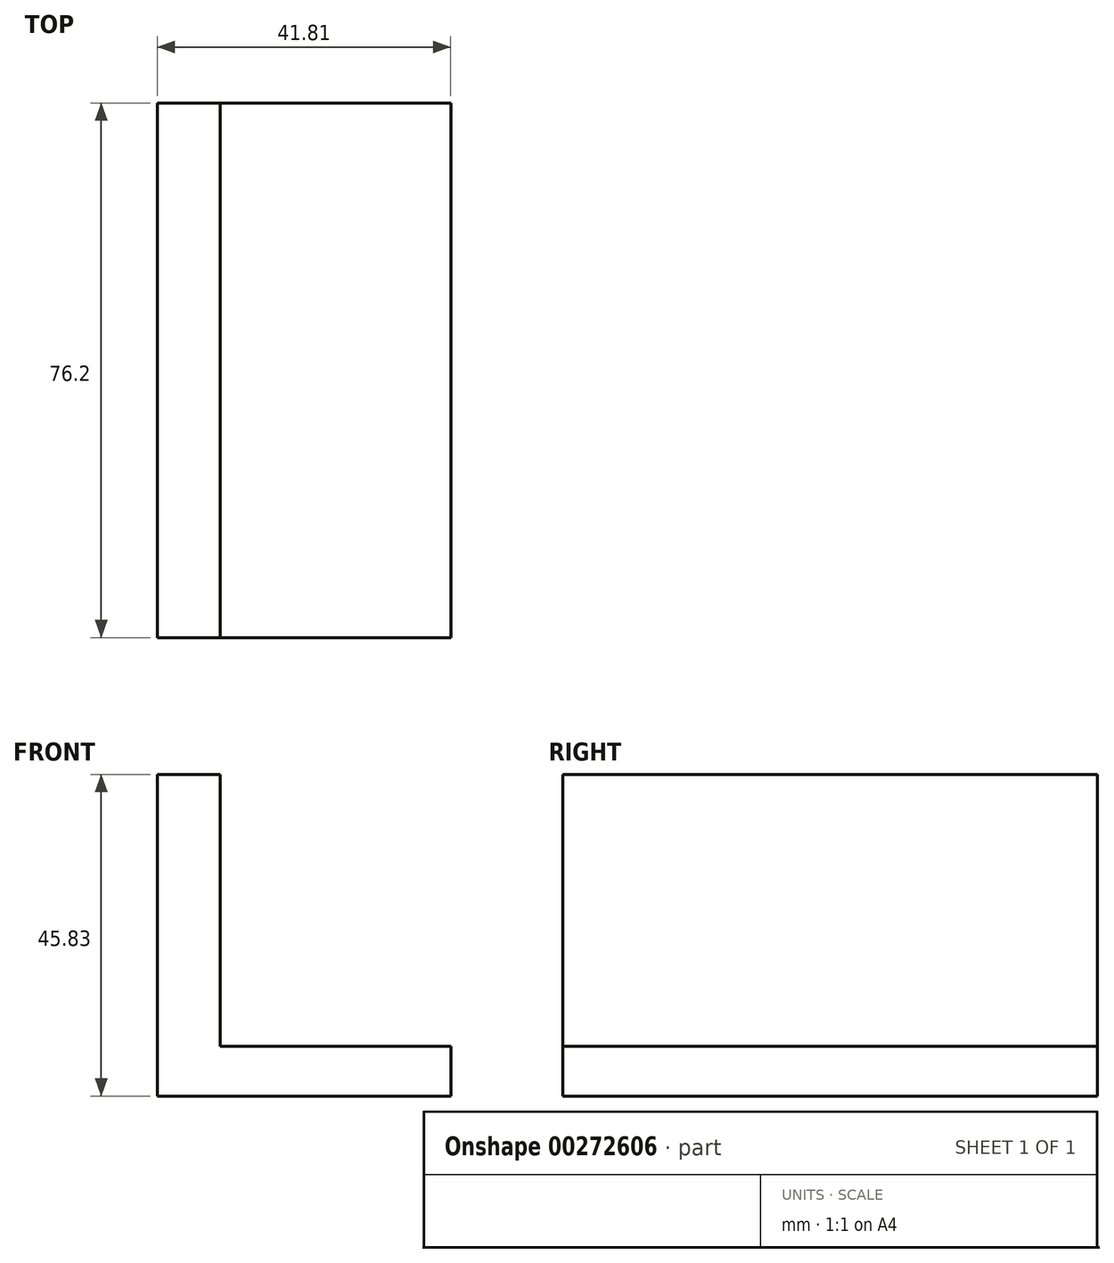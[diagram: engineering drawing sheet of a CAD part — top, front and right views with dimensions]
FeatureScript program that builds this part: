
annotation { "Feature Type Name" : "Feature", "Feature Type Description" : "" }
export const myFeature = defineFeature(function(context is Context, id is Id, definition is map)
    precondition{}
    {
        {
            var Q0;
            Q0=qCreatedBy(makeId("Front.planeOp"),FACE);
            var sketch = newSketch(context, id + "F0", { "sketchPlane" : qUnion([Q0])});
            skLineSegment(sketch, "E0", {"start": v(0, 0) * mm, "end": v(0, 38.76) * mm});
            skLineSegment(sketch, "E1", {"start": v(0, 0) * mm, "end": v(32.84, 0) * mm});
            skLineSegment(sketch, "E2", {"start": v(32.84, 0) * mm, "end": v(32.84, -7.07) * mm});
            skLineSegment(sketch, "E3", {"start": v(32.84, -7.07) * mm, "end": v(-8.97, -7.07) * mm});
            skLineSegment(sketch, "E4", {"start": v(-8.97, -7.07) * mm, "end": v(-8.97, 38.76) * mm});
            skLineSegment(sketch, "E5", {"start": v(-8.97, 38.76) * mm, "end": v(0, 38.76) * mm});
            skSolve(sketch);
        }
        {
            var Q0;
            Q0 = qSketchRegion(id + "F0", true);
            extrude(context, id + "F1", {"entities" : qUnion([Q0]), "depth" : 76.2 * mm});
        }
    });
